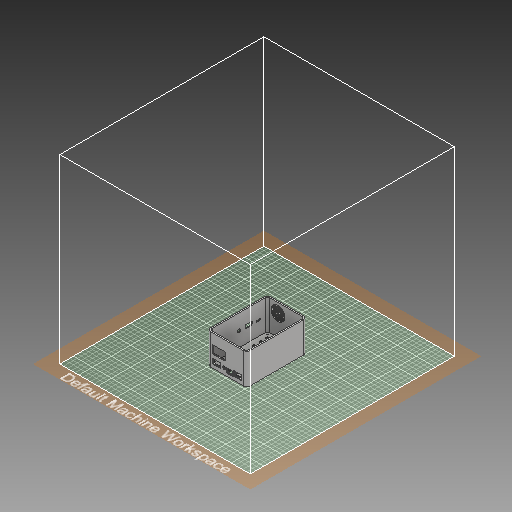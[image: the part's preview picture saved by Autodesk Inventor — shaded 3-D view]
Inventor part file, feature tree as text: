
AUTODESK INVENTOR PART (.ipt)
format: ipt  version: 2019 (Build 230136000, 136)  size: 1,141,760 bytes
history: native  units: in
note: dims shown in document units (in); Inventor stores cm internally (conversion verified against a paired STEP export)
features: sketch x15, extrude x11, fillet x9, shell x1, other x1
ambient origin geometry x8: Origin, YZ Plane, XZ Plane, XY Plane, X Axis, Y Axis, Z Axis, Center Point
bodies: Solid1 (feature_tree)
feature tree (37):
  extrude  "Extrusion1"  Depth=5.0in
  shell  "Shell1"  Thickness=0.1969in
  fillet  "Fillet1"  Radius=2.6181in
  extrude  "Extrusion2"  Depth=0.0787in
  sketch  "Sketch4"  dims[d7=0.378in d8=0.0in]
  sketch  "Sketch5"  dims[d9=0.315in d10=0.6299in]
  extrude  "Extrusion4"  TaperAngle=0.0deg  [1 undecoded]
  extrude  "Extrusion5"  Depth=0.6299in
  extrude  "Extrusion7"  Depth=0.3543in
  extrude  "Extrusion8"  Depth=0.315in
  fillet  "Fillet2"  Radius=2.3622in
  fillet  "Fillet3"  Radius=0.6299in
  fillet  "Fillet4"  Radius=0.3543in
  sketch  "Sketch15"  dims[d29=0.3209in d30=0.0591in d31=0.0in d32=0.7283in d33=1.2205in]
  sketch  "Sketch16"  dims[d34=0.3543in d37=0.6299in d38=0.2953in d39=0.5118in]
  extrude  "Extrusion13"  Depth=0.248in
  fillet  "Fillet7"  Radius=0.4724in
  extrude  "Extrusion14"  Depth=0.0591in TaperAngle=0.0deg
  fillet  "Fillet8"  Radius=0.7283in
  fillet  "Fillet9"  Radius=1.2205in
  extrude  "Extrusion15"  Depth=0.6299in
  fillet  "Fillet10"  Radius=0.2953in
  fillet  "Fillet11"  Radius=0.5118in
  other  "Grill1"
  extrude  "Extrusion18"  Depth=0.2756in
  extrude  "Extrusion19"  Depth=0.0787in
  sketch  "Sketch1"  dims[d0=3.189in d1=5.0in d2=0.1969in d3=2.6181in d4=0.0in]
  sketch  "Sketch2"  dims[d5=0.1181in d6=0.0787in]
  sketch  "Sketch6"  dims[d11=90.0deg d12=0.3543in]
  sketch  "Sketch13"  dims[d13=0.378in d14=0.315in d16=2.3622in d17=0.0in d24=0.6299in d25=0.3543in]
  sketch  "Sketch14"  dims[d26=0.1476in d27=0.248in d28=0.4724in]
  sketch  "Sketch24"  dims[d40=0.1181in d41=0.2756in]
  sketch  "Sketch25"  dims[d42=0.0591in d43=0.0in d54=0.0787in]
  sketch  "Sketch26"  dims[d56=0.0787in]
  sketch  "Sketch30"  dims[d57=0.0787in]
  sketch  "Sketch32"  dims[d58=0.0394in]
  sketch  "Sketch33"  dims[d59=0.0394in d62=0.3346in d63=0.1772in d64=0.1969in d65=0.5906in d66=0.0in d67=0.4724in d68=0.4724in d69=0.1575in d71=0.4724in d72=0.2756in d73=0.4724in d74=0.0787in d75=0.0787in d76=0.5906in d77=0.0in d78=0.0787in d79=0.0394in d80=0.0394in d83=0.0394in d148=0.1969in d149=0.3937in d150=0.1969in d151=0.3937in d152=0.1969in d153=0.3937in d154=0.1969in d157=0.3937in d158=0.0in d159=0.0787in d161=0.1575in d162=0.1575in d163=0.1575in d164=0.1575in d167=0.1575in d168=0.1575in d169=0.0787in d170=0.0in d171=0.0787in d172=0.0787in d173=0.3937in d174=0.6299in d175=0.0787in d176=0.0in d177=0.0394in d189=1.122in d190=0.9843in d191=0.0787in d194=0.2362in d195=0.1181in d196=1.1811in d197=1.1811in d198=2.3622in d200=0.1969in d201=0.3937in d203=0.3937in d205=2.3622in d207=0.1969in d208=0.3937in d210=0.3937in d212=0.0394in d213=0.1181in d214=0.0in d215=0.0394in d216=0.1181in d217=0.0in d218=0.0394in d219=0.0in d220=0.0in d221=0.0394in d222=0.0in d223=0.0in d224=0.0in d225=1.8479in d228=1.0236in d229=0.0394in d230=0.0394in d231=1.1024in d232=0.7087in d233=0.0394in d234=0.0in d235=0.3543in d236=0.0787in d237=0.0787in d239=0.0591in d240=0.0in]
note: 1 required parameter value undecoded (feature->parameter linkage not recoverable at this tier; creation-order binding heuristic only, values carry confidence <= 0.55)
